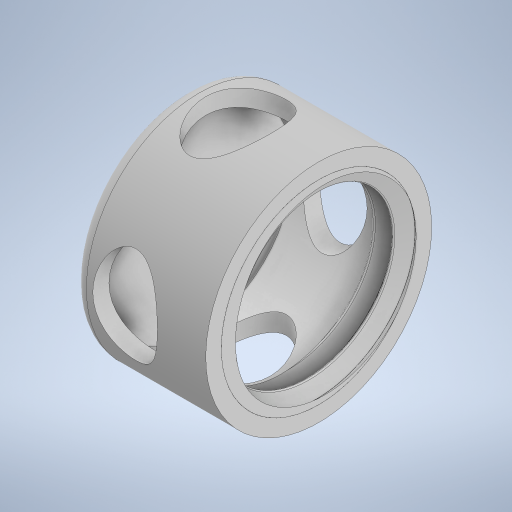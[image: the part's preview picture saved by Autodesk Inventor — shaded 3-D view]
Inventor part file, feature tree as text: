
AUTODESK INVENTOR PART (.ipt)
format: ipt  version: 2023 (Build 270158000, 158)  size: 495,616 bytes
history: native  units: in
note: dims shown in document units (in); Inventor stores cm internally (conversion verified against a paired STEP export)
features: sketch x6, extrude x5, fillet x1, thread x1, revolve x1, helix x1
ambient origin geometry x8: Origin, YZ Plane, XZ Plane, XY Plane, X Axis, Y Axis, Z Axis, Center Point
bodies: Solid1 (feature_tree), Solid11 (feature_tree)
feature tree (15):
  sketch  "Sketch1"  dims[d0=1.1811in d1=1.378in]
  extrude  "Extrusion2"  Depth=1.378in
  sketch  "Sketch2"  dims[d4=0.0591in d5=0.0in d6=0.1969in]
  sketch  "Sketch3"  dims[d7=0.2953in d8=0.315in]
  extrude  "Extrusion3"  Depth=0.1969in
  extrude  "Extrusion4"  Depth=0.315in
  extrude  "Extrusion5"  Depth=0.2953in
  fillet  "Fillet1"  Radius=0.315in
  extrude  "Extrusion7"  Depth=0.8071in TaperAngle=0.0deg
  thread  "Thread10"  [1 undecoded]
  revolve  "Revolution10"  [1 undecoded]
  helix  "Coil10"  [1 undecoded]
  sketch  "Sketch8"  dims[d9=0.1969in d10=0.2953in d11=0.315in]
  sketch  "Sketch23"  dims[d12=0.8071in d13=0.0in d14=1.5748in d15=0.0in d16=1.5748in d17=0.0in]
  sketch  "Sketch24"  dims[d27=0.3779in d38=0.0787in d48=0.3779in d59=1.189in d71=0.3779in d92=0.3779in d103=0.1969in d104=0.0in d114=0.3779in d134=0.3779in d154=0.3779in d176=0.3779in d196=0.3779in d207=0.1969in d208=0.0in d209=0.3779in d210=0.0189in d211=0.0189in d214=0.1232in d216=0.3779in d218=0.0in d219=0.1182in d220=0.4331in d221=0.3937in d222=0.0in d223=0.0in d224=0.0in d225=0.0in d226=0.0in]
note: 3 required parameter values undecoded (feature->parameter linkage not recoverable at this tier; creation-order binding heuristic only, values carry confidence <= 0.55)